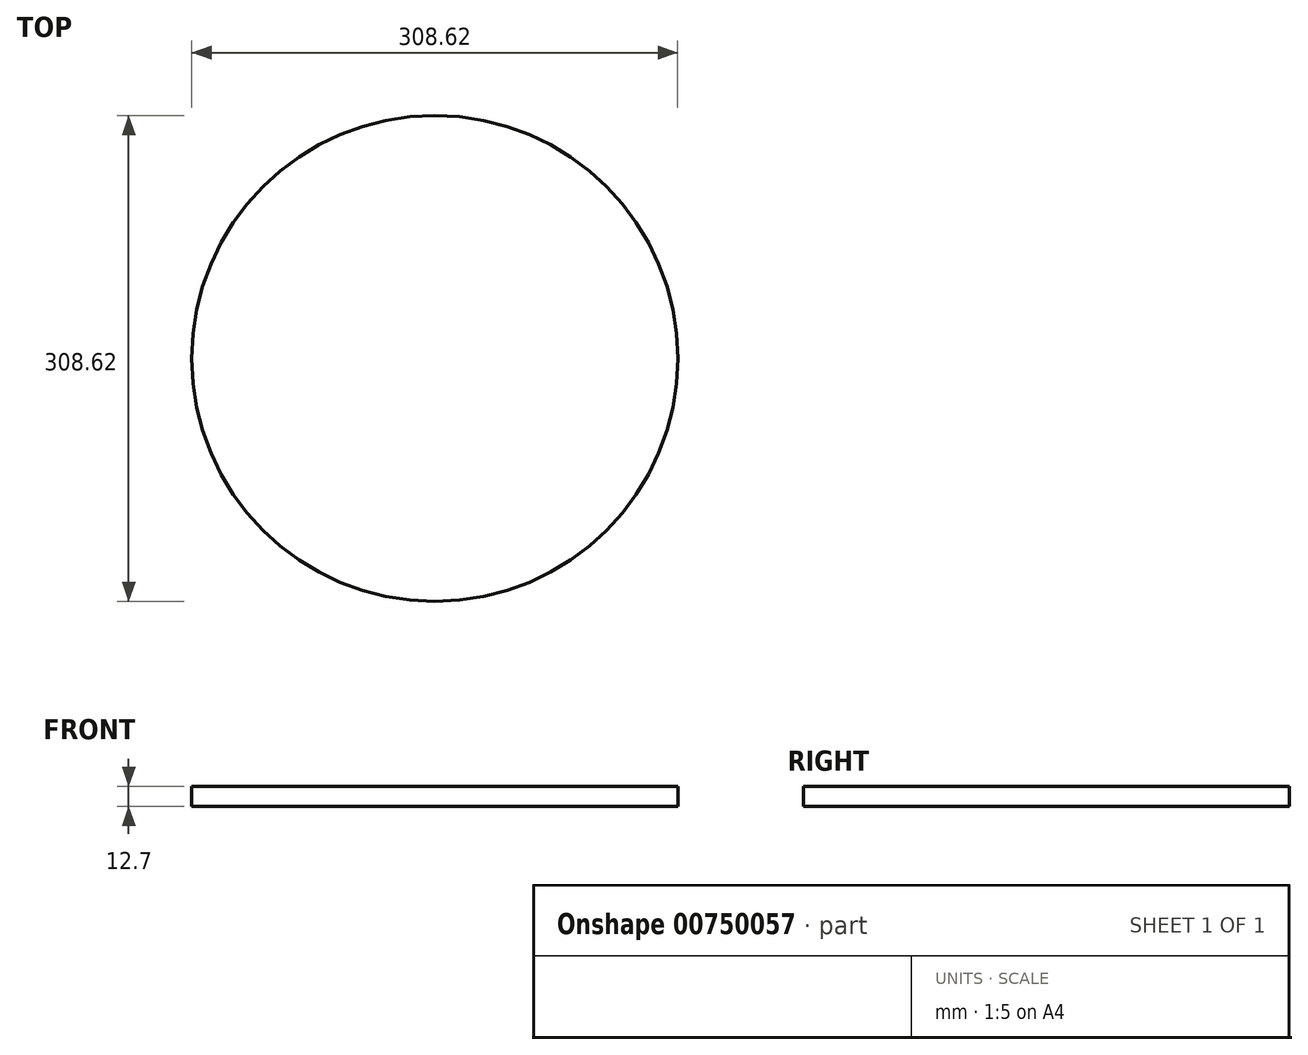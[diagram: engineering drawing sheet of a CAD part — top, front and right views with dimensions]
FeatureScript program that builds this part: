
annotation { "Feature Type Name" : "Feature", "Feature Type Description" : "" }
export const myFeature = defineFeature(function(context is Context, id is Id, definition is map)
    precondition{}
    {
        {
            var Q0;
            Q0=qCreatedBy(makeId("Top.planeOp"),FACE);
            var sketch = newSketch(context, id + "F0", { "sketchPlane" : qUnion([Q0])});
            skCircle(sketch, "E0", {"center": v(-4.38, 10.85) * mm, "radius": 154.31 * mm});
            skSolve(sketch);
        }
        {
            var Q0;
            Q0=makeQuery(id+"F0.imprint","IMPRINT",FACE,{"disambiguationData":[TD([[makeQuery(id+"F0.imprint","IMPRINT",EDGE,{"derivedFrom":sQuery(id+"F0.wireOp",EDGE,"E0")}),1.0]])]});
            extrude(context, id + "F1", {"entities" : qUnion([Q0]), "depth" : 12.7 * mm, "offsetDistance" : 25.4 * mm});
        }
    });
